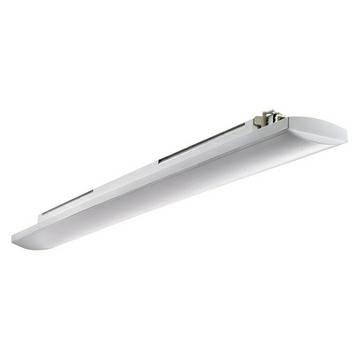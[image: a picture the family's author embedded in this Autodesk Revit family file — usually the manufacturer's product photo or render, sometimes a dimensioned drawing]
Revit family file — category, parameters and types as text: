
# Revit family: Lighting-Industriale-GEWISS-SMART[3]PLUS-PLAFONIERA-LED-EMERGENZA_OPALE_1200mm
name_source: partatom
category: Apparecchi per illuminazione
units: mm (PartAtom-declared; Revit-internal decimal feet)

## family parameters
Condiviso = No
Host = Superficie
Numero OmniClass = 23.80.70.11
Punto di calcolo locali = No
Quota connettore circolare = Usa diametro
Sorgente d'illuminazione = No
Taglio con vuoti quando caricato = No
Tipo di parte = Normale
Titolo OmniClass = Luminaries for Internal Lighting

## types (1)
- Lighting-Industriale-GEWISS-SMART[3]PLUS-PLAFONIERA-LED-EMERGENZA_OPALE_1200mm
    Applicazione = Interno
    Carico apparente = 45 VA
    Catalogo = LIGHTING
    Catalogo Serie = SMART[3] PLUS
    Classe di efficienza LED integrati = A ÷ A++
    Classe isolamento = II
    Codice Electrocod = 2434
    Commenti sul wattaggio = 45W
    Descrizione = SMART3 PLUS 1200 EMERG DT1+DT6 HE OPAL 9 57
    Ganci = GEWISS  - ALLUMINIO
    Garanzia = ND
    Glow Wire Test = 850°C
    Grado di protezione = IP66/IP69
    IDF = 40e73a22-c19b-474b-9c80-f3130e384cc5
    IDT = c24490b2-922b-4a62-9750-73ed8a6aae65
    Immagine tipo = GWS3136P.jpg
    Lampada = LED
    Lampada: = LED
    Lumen output (lm) = 3900
    Lunghezza = 1200 mm
    Lunghezza Lampada = 1200 mm
    Modello = GWS3225AP957
    Potenza di sistema = 36 W
    Produttore = GEWISS S.p.A.
    Prospetto di default = 1219 mm
    Resistenza agli urti = IK08
    SEO = Plafoniera
    Scheda Tecnica = https://www.gewiss.com
    Schermo = Opale
    Schermo. = Gewiss - Led Acceso
    Stampa 1_100 = Sì
    Stampa 1_200 = No
    Struttura = GEWISS - SMART 3 - GRIGIO
    Temperatura di colore = 5700 K (CRI > 90)
    Temperatura di colore: = 5700 K (CRI > 90)
    Temperatura di funzionamento = ND
    Temperatura di utilizzo = ND
    Tensione = 220-240 V
    Tipologia sorgente luminosa = LED - Non sostituibile
    URL = https://www.gewiss.com
    Versione file RFA = 20.0
